# Revit family: Building-ContenitoriIncasso-GEWISS-48PTC-CENTRALINI-COMBINATI-IP55
name_source: partatom
category: Attrezzatura elettrica
revit_build: Autodesk Revit 2016 (Build: 20161004_0715(x64)
units: mm (PartAtom-declared; Revit-internal decimal feet)

## family parameters
Condiviso = No
Configurazione quadro = Due colonne, circuiti in orizzontale
Host = Muro
Numero OmniClass = 23.60.00.00
Punto di calcolo locali = No
Quota connettore circolare = Usa diametro
Sempre verticale = Sì
Taglio con vuoti quando caricato = No
Tipo di parte = Pannello comandi
Titolo OmniClass = General Purpose: Services

## types (1)
- GW48686 - QUADRETTO COMB.INC.4M+2FL.IP55 GR7035
    Carico = Altro
    Catalogo = BUILDING
    Catalogo Serie = 48 PTC
    Classe isolamento = II (secondo Norma IEC 61140)
    Codice EAN = 8011564071728
    Codice Electrocod = 1320
    Colore = Grigio RAL 7035
    Colore coperchio = Grigio RAL 7035
    Colore porta = Trasparente fume'
    Descrizione = QUADRETTO COMB.INC.4M+2FL.IP55 GR7035
    Dim. esterne BxHxP (mm) = 308x169x70
    Dim. frontale BxH (mm) = 345x210
    Glow Wire Test = 650°C
    Grado di protezione = IP55
    H_da terra = 922 mm
    IDF = 0a11316e-1d5c-4f0e-8c2f-68eebb2b26da
    IDT = d60fa815-1ed1-451d-83db-3132591f839a
    Immagine tipo = GW48686.jpg
    Installazione = Incasso
    Modello = GW48686
    N. mod. EN 50022 = 4
    Numero di poli = 1
    Potenza = 0 V
    Potenza dissipabile (W) = 19
    Produttore = GEWISS S.p.A.
    Resistenza agli urti = IK08
    SEO = Quadretto
    Scheda Tecnica = https://www.gewiss.com
    Temperatura di impiego = -15 +60 °C
    Termopressione con biglia = 70 °C
    Tipo Materiale = Halogen free secondo norma EN 60754-2
    URL = https://www.gewiss.com
    Versione file RFA = 18.0
